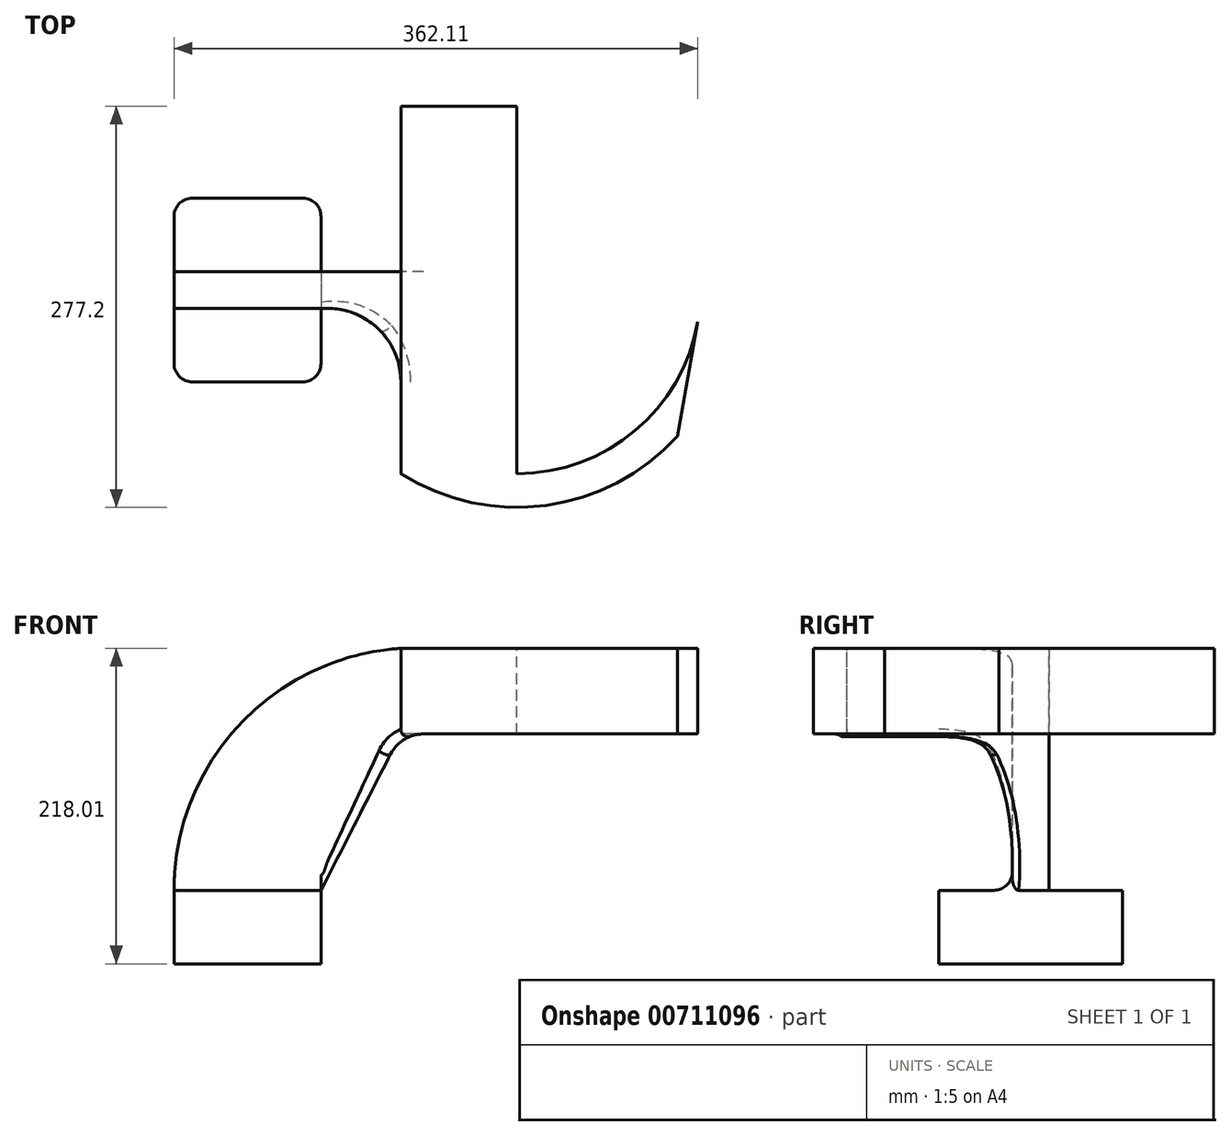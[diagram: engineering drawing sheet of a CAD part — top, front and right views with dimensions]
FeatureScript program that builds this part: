
annotation { "Feature Type Name" : "Feature", "Feature Type Description" : "" }
export const myFeature = defineFeature(function(context is Context, id is Id, definition is map)
    precondition{}
    {
        {
            var Q0;
            Q0=qCreatedBy(makeId("Front.planeOp"),FACE);
            var sketch = newSketch(context, id + "F0", { "sketchPlane" : qUnion([Q0])});
            skLineSegment(sketch, "E0.bottom", {"start": v(50.8, 25.4) * mm, "end": v(-50.8, 25.4) * mm});
            skLineSegment(sketch, "E0.top", {"start": v(50.8, -25.4) * mm, "end": v(-50.8, -25.4) * mm});
            skLineSegment(sketch, "E0.left", {"start": v(50.8, 25.4) * mm, "end": v(50.8, -25.4) * mm});
            skLineSegment(sketch, "E0.right", {"start": v(-50.8, 25.4) * mm, "end": v(-50.8, -25.4) * mm});
            skPoint(sketch, "E0.middle", {"position": v(0, 0) * mm});
            skLineSegment(sketch, "E1.bottom", {"start": v(186.24, 133.43) * mm, "end": v(106.05, 133.43) * mm});
            skLineSegment(sketch, "E1.top", {"start": v(186.24, 192.6) * mm, "end": v(106.05, 192.6) * mm});
            skLineSegment(sketch, "E1.left", {"start": v(186.24, 133.43) * mm, "end": v(186.24, 192.6) * mm});
            skLineSegment(sketch, "E1.right", {"start": v(106.05, 133.43) * mm, "end": v(106.05, 192.6) * mm});
            skPoint(sketch, "E1.middle", {"position": v(146.14, 163.02) * mm});
            skLineSegment(sketch, "E2", {"start": v(50.8, 25.4) * mm, "end": v(106.05, 133.43) * mm});
            skArc(sketch, "E3", {"start": v(-50.8, 25.4) * mm, "mid": v(-5.45, 140.03) * mm, "end": v(106.05, 192.6) * mm});
            skFitSpline(sketch, "E4", {"points": [v(50.8, -25.4) * mm, v(186.24, 133.43) * mm, v(186.24, 192.6) * mm], "startDerivative": vector(303.2, 233.54) * mm, "endDerivative": vector(-275.87, 267.12) * mm});
            skSolve(sketch);
        }
        {
            var Q0;
            Q0=makeQuery(id+"F0.imprint","IMPRINT",FACE,{"disambiguationData":[TD([[makeQuery(id+"F0.imprint","IMPRINT",EDGE,{"derivedFrom":sQuery(id+"F0.wireOp",EDGE,"E0.bottom")}),1.0]])]});
            extrude(context, id + "F1", {"entities" : qUnion([Q0]), "endBound" : BoundingType.SYMMETRIC, "oppositeDirection" : true, "depth" : 127 * mm, "offsetDistance" : 25.4 * mm});
        }
        {
            var Q0;
            Q0=makeQuery(id+"F0.imprint","IMPRINT",FACE,{"disambiguationData":[TD([[makeQuery(id+"F0.imprint","IMPRINT",EDGE,{"derivedFrom":sQuery(id+"F0.wireOp",EDGE,"E0.bottom")}),-1.0]])]});
            extrude(context, id + "F2", {"entities" : qUnion([Q0]), "operationType" : NewBodyOperationType.ADD, "endBound" : BoundingType.SYMMETRIC, "oppositeDirection" : true, "depth" : 25.4 * mm, "offsetDistance" : 25.4 * mm});
        }
        {
            var Q0;
            Q0=makeQuery(id+"F0.imprint","IMPRINT",FACE,{"disambiguationData":[TD([[makeQuery(id+"F0.imprint","IMPRINT",EDGE,{"derivedFrom":sQuery(id+"F0.wireOp",EDGE,"E1.bottom")}),-1.0]])]});
            extrude(context, id + "F3", {"entities" : qUnion([Q0]), "operationType" : NewBodyOperationType.ADD, "endBound" : BoundingType.SYMMETRIC, "depth" : 254 * mm, "offsetDistance" : 25.4 * mm});
        }
        {
            var Q0;
            Q0=makeQuery(id+"F3.opExtrude","CAP_FACE",FACE,{"disambiguationData":[OSD([sQuery(id+"F0.wireOp",EDGE,"E1.bottom"),sQuery(id+"F0.wireOp",EDGE,"E1.top"),sQuery(id+"F0.wireOp",EDGE,"E1.left"),sQuery(id+"F0.wireOp",EDGE,"E1.right")])],"isStart":false});
            var Q1;
            Q1=sQuery(id+"F0.wireOp",EDGE,"E1.left");
            revolve(context, id + "F4", {"operationType" : NewBodyOperationType.ADD, "surfaceOperationType" : NewSurfaceOperationType.NEW, "entities" : qUnion([Q0]), "axis" : qUnion([Q1]), "revolveType" : RevolveType.ONE_DIRECTION, "angle" : 80 * degree});
        }
        {
            var Q0;
            Q0=makeQuery(id+"F1.opExtrude","CAP_EDGE",EDGE,{"disambiguationData":[OSD([sQuery(id+"F0.wireOp",EDGE,"E0.left")])],"isStart":true});
            var Q1;
            Q1=makeQuery(id+"F1.opExtrude","CAP_EDGE",EDGE,{"disambiguationData":[OSD([sQuery(id+"F0.wireOp",EDGE,"E0.right")])],"isStart":true});
            var Q2;
            Q2=makeQuery(id+"F2.opExtrude","CAP_EDGE",EDGE,{"disambiguationData":[OSD([sQuery(id+"F0.wireOp",EDGE,"E0.bottom")])],"isStart":true});
            var Q3;
            Q3=makeQuery(id+"F2.opExtrude","CAP_EDGE",EDGE,{"disambiguationData":[OSD([sQuery(id+"F0.wireOp",EDGE,"E0.bottom")])],"isStart":false});
            var Q4;
            Q4=makeQuery(id+"F1.opExtrude","CAP_EDGE",EDGE,{"disambiguationData":[OSD([sQuery(id+"F0.wireOp",EDGE,"E0.right")])],"isStart":false});
            var Q5;
            Q5=makeQuery(id+"F1.opExtrude","CAP_EDGE",EDGE,{"disambiguationData":[OSD([sQuery(id+"F0.wireOp",EDGE,"E0.left")])],"isStart":false});
            fillet(context, id + "F5", {"entities" : qUnion([Q0, Q1, Q2, Q3, Q4, Q5]), "radius" : 12.7 * mm, "tangentPropagation" : true, "allowEdgeOverflow" : false});
        }
        {
            var Q0;
            Q0=makeQuery(id+"F2.opExtrude","CAP_EDGE",EDGE,{"disambiguationData":[OSD([sQuery(id+"F0.wireOp",EDGE,"E1.right")])],"isStart":false});
            var Q1;
            Q1=makeQuery(id+"F2.opExtrude","CAP_EDGE",EDGE,{"disambiguationData":[OSD([sQuery(id+"F0.wireOp",EDGE,"E1.right")])],"isStart":true});
            fillet(context, id + "F6", {"entities" : qUnion([Q0, Q1]), "radius" : 50.8 * mm, "tangentPropagation" : true, "allowEdgeOverflow" : false});
        }
        {
            var Q0;
            {var subQ0=sQuery(id+"F0.wireOp",EDGE,"E2");var subQ1=sQuery(id+"F0.wireOp",EDGE,"E1.right");var subQ2=sQuery(id+"F0.wireOp",EDGE,"E1.bottom");Q0=makeQuery(id+"F3.boolean.opBoolean","MERGE",EDGE,{"derivedFrom":[makeQuery(id+"F2.opExtrude","SWEPT_EDGE",EDGE,{"disambiguationData":[OSD([subQ2,subQ1,subQ0])]}),makeQuery(id+"F3.opExtrude","SWEPT_EDGE",EDGE,{"disambiguationData":[OSD([subQ2,subQ1,subQ0])]})]});}
            fillet(context, id + "F7", {"entities" : qUnion([Q0]), "radius" : 25.4 * mm, "tangentPropagation" : true, "allowEdgeOverflow" : false});
        }
        {
            var Q0;
            Q0=makeQuery(id+"F6.opFillet","BLEND_EDGE",EDGE,{"blendedFrom":[makeQuery(id+"F2.opExtrude","CAP_EDGE",EDGE,{"disambiguationData":[OSD([sQuery(id+"F0.wireOp",EDGE,"E1.right")])],"isStart":true}),makeQuery(id+"F2.opExtrude","SWEPT_FACE",FACE,{"disambiguationData":[OSD([sQuery(id+"F0.wireOp",EDGE,"E2")])]})],"blendedInto":[makeQuery(id+"F2.opExtrude","SWEPT_FACE",FACE,{"disambiguationData":[OSD([sQuery(id+"F0.wireOp",EDGE,"E2")])]})]});
            var Q1;
            Q1=makeQuery(id+"F6.opFillet","BLEND_EDGE",EDGE,{"blendedFrom":[makeQuery(id+"F2.opExtrude","CAP_EDGE",EDGE,{"disambiguationData":[OSD([sQuery(id+"F0.wireOp",EDGE,"E1.right")])],"isStart":false}),makeQuery(id+"F2.opExtrude","SWEPT_FACE",FACE,{"disambiguationData":[OSD([sQuery(id+"F0.wireOp",EDGE,"E2")])]})],"blendedInto":[makeQuery(id+"F2.opExtrude","SWEPT_FACE",FACE,{"disambiguationData":[OSD([sQuery(id+"F0.wireOp",EDGE,"E2")])]})]});
            var Q2;
            {var subQ0=sQuery(id+"F0.wireOp",EDGE,"E1.right");var subQ1=sQuery(id+"F0.wireOp",EDGE,"E2");var subQ2=sQuery(id+"F0.wireOp",EDGE,"E1.bottom");Q2=makeQuery(id+"F7.opFillet","BLEND_EDGE",EDGE,{"blendedFrom":[makeQuery(id+"F3.boolean.opBoolean","MERGE",EDGE,{"derivedFrom":[makeQuery(id+"F2.opExtrude","SWEPT_EDGE",EDGE,{"disambiguationData":[OSD([subQ2,subQ0,subQ1])]}),makeQuery(id+"F3.opExtrude","SWEPT_EDGE",EDGE,{"disambiguationData":[OSD([subQ2,subQ0,subQ1])]})]}),makeQuery(id+"F6.opFillet","BLEND_FACE",FACE,{"disambiguationData":[OSD([subQ0]),TDD([makeQuery(id+"F2.opExtrude","CAP_EDGE",EDGE,{"disambiguationData":[OSD([subQ0])],"isStart":true})])]})],"blendedInto":[makeQuery(id+"F6.opFillet","BLEND_FACE",FACE,{"disambiguationData":[OSD([subQ0]),TDD([makeQuery(id+"F2.opExtrude","CAP_EDGE",EDGE,{"disambiguationData":[OSD([subQ0])],"isStart":true})])]})]});}
            var Q3;
            {var subQ0=sQuery(id+"F0.wireOp",EDGE,"E1.bottom");var subQ1=sQuery(id+"F0.wireOp",EDGE,"E3");var subQ2=sQuery(id+"F0.wireOp",EDGE,"E2");var subQ3=sQuery(id+"F0.wireOp",EDGE,"E1.right");Q3=makeQuery(id+"F7.opFillet","BLEND_EDGE",EDGE,{"blendedFrom":[makeQuery(id+"F3.boolean.opBoolean","MERGE",EDGE,{"derivedFrom":[makeQuery(id+"F2.opExtrude","SWEPT_EDGE",EDGE,{"disambiguationData":[OSD([subQ0,subQ3,subQ2])]}),makeQuery(id+"F3.opExtrude","SWEPT_EDGE",EDGE,{"disambiguationData":[OSD([subQ0,subQ3,subQ2])]})]}),makeQuery(id+"F3.boolean.opBoolean","SPLIT",FACE,{"disambiguationData":[TD([makeQuery(id+"F2.opExtrude","CAP_FACE",FACE,{"disambiguationData":[OSD([sQuery(id+"F0.wireOp",EDGE,"E0.bottom"),subQ3,subQ2,subQ1])],"isStart":true})])],"derivedFrom":makeQuery(id+"F3.opExtrude","SWEPT_FACE",FACE,{"disambiguationData":[OSD([subQ3])]})})],"blendedInto":[makeQuery(id+"F3.boolean.opBoolean","SPLIT",FACE,{"disambiguationData":[TD([makeQuery(id+"F2.opExtrude","CAP_FACE",FACE,{"disambiguationData":[OSD([sQuery(id+"F0.wireOp",EDGE,"E0.bottom"),subQ3,subQ2,subQ1])],"isStart":true})])],"derivedFrom":makeQuery(id+"F3.opExtrude","SWEPT_FACE",FACE,{"disambiguationData":[OSD([subQ3])]})})]});}
            var Q4;
            {var subQ0=sQuery(id+"F0.wireOp",EDGE,"E1.right");var subQ1=sQuery(id+"F0.wireOp",EDGE,"E2");var subQ2=sQuery(id+"F0.wireOp",EDGE,"E1.bottom");Q4=makeQuery(id+"F7.opFillet","BLEND_EDGE",EDGE,{"blendedFrom":[makeQuery(id+"F3.boolean.opBoolean","MERGE",EDGE,{"derivedFrom":[makeQuery(id+"F2.opExtrude","SWEPT_EDGE",EDGE,{"disambiguationData":[OSD([subQ2,subQ0,subQ1])]}),makeQuery(id+"F3.opExtrude","SWEPT_EDGE",EDGE,{"disambiguationData":[OSD([subQ2,subQ0,subQ1])]})]}),makeQuery(id+"F6.opFillet","BLEND_FACE",FACE,{"disambiguationData":[OSD([subQ0]),TDD([makeQuery(id+"F2.opExtrude","CAP_EDGE",EDGE,{"disambiguationData":[OSD([subQ0])],"isStart":false})])]})],"blendedInto":[makeQuery(id+"F6.opFillet","BLEND_FACE",FACE,{"disambiguationData":[OSD([subQ0]),TDD([makeQuery(id+"F2.opExtrude","CAP_EDGE",EDGE,{"disambiguationData":[OSD([subQ0])],"isStart":false})])]})]});}
            var Q5;
            {var subQ0=sQuery(id+"F0.wireOp",EDGE,"E3");var subQ1=sQuery(id+"F0.wireOp",EDGE,"E2");var subQ2=sQuery(id+"F0.wireOp",EDGE,"E1.bottom");var subQ3=sQuery(id+"F0.wireOp",EDGE,"E1.right");Q5=makeQuery(id+"F7.opFillet","BLEND_EDGE",EDGE,{"blendedFrom":[makeQuery(id+"F3.boolean.opBoolean","MERGE",EDGE,{"derivedFrom":[makeQuery(id+"F2.opExtrude","SWEPT_EDGE",EDGE,{"disambiguationData":[OSD([subQ2,subQ3,subQ1])]}),makeQuery(id+"F3.opExtrude","SWEPT_EDGE",EDGE,{"disambiguationData":[OSD([subQ2,subQ3,subQ1])]})]}),makeQuery(id+"F3.boolean.opBoolean","SPLIT",FACE,{"disambiguationData":[TD([makeQuery(id+"F2.opExtrude","CAP_FACE",FACE,{"disambiguationData":[OSD([sQuery(id+"F0.wireOp",EDGE,"E0.bottom"),subQ3,subQ1,subQ0])],"isStart":false})])],"derivedFrom":makeQuery(id+"F3.opExtrude","SWEPT_FACE",FACE,{"disambiguationData":[OSD([subQ3])]})})],"blendedInto":[makeQuery(id+"F3.boolean.opBoolean","SPLIT",FACE,{"disambiguationData":[TD([makeQuery(id+"F2.opExtrude","CAP_FACE",FACE,{"disambiguationData":[OSD([sQuery(id+"F0.wireOp",EDGE,"E0.bottom"),subQ3,subQ1,subQ0])],"isStart":false})])],"derivedFrom":makeQuery(id+"F3.opExtrude","SWEPT_FACE",FACE,{"disambiguationData":[OSD([subQ3])]})})]});}
            fillet(context, id + "F8", {"entities" : qUnion([Q0, Q1, Q2, Q3, Q4, Q5]), "radius" : 5.08 * mm, "tangentPropagation" : true, "allowEdgeOverflow" : false});
        }
    });
